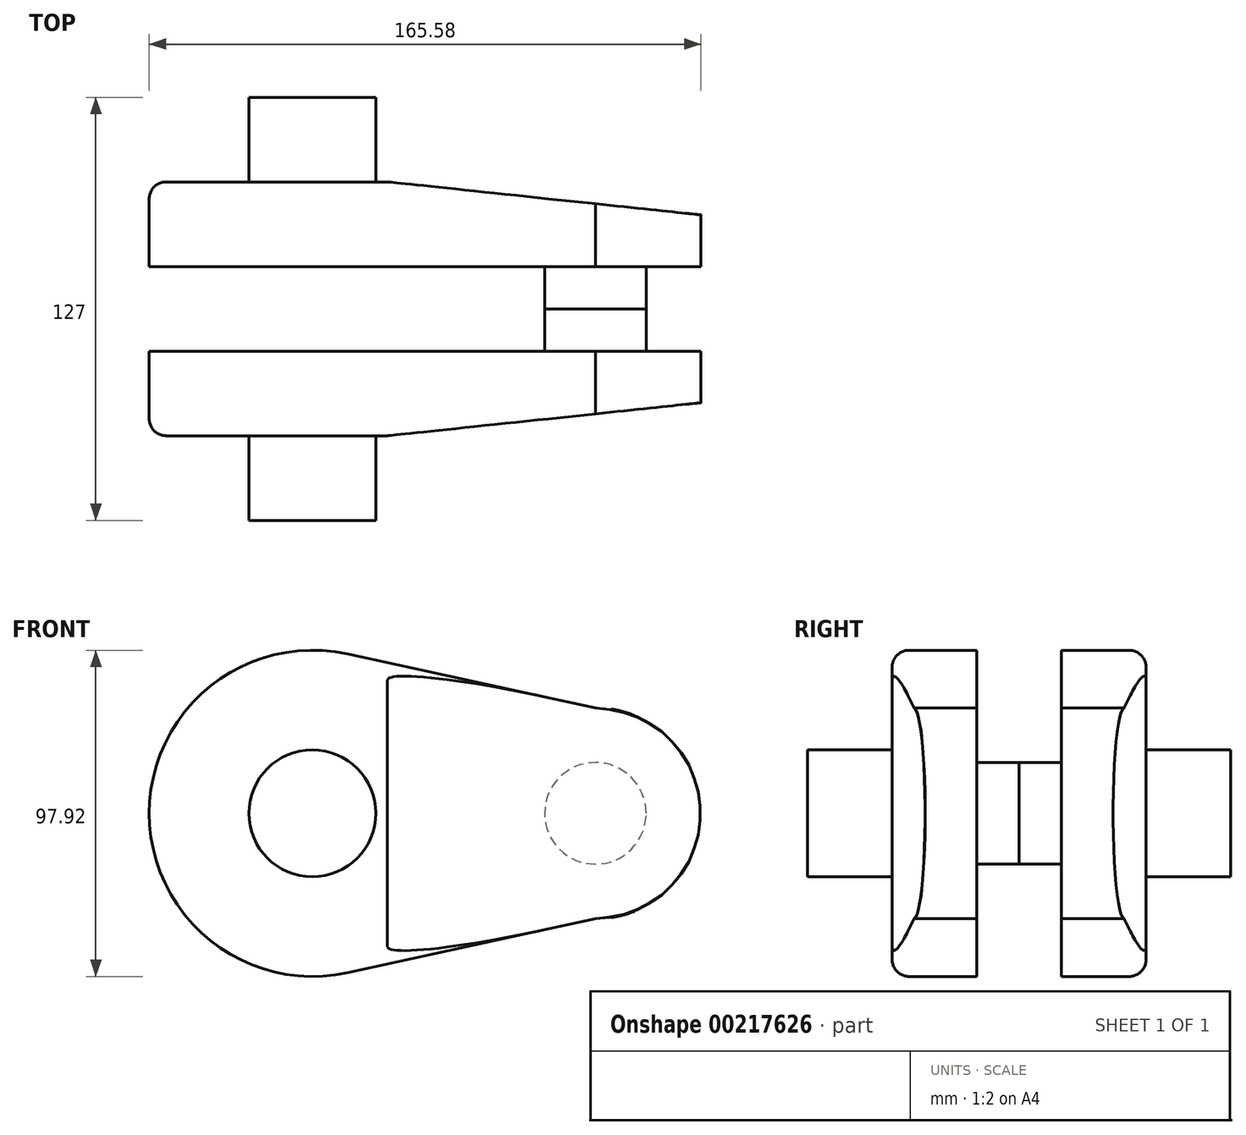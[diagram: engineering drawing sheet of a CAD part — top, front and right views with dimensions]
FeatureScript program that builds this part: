
annotation { "Feature Type Name" : "Feature", "Feature Type Description" : "" }
export const myFeature = defineFeature(function(context is Context, id is Id, definition is map)
    precondition{}
    {
        {
            var Q0;
            Q0=qCreatedBy(makeId("Front.planeOp"),FACE);
            var sketch = newSketch(context, id + "F0", { "sketchPlane" : qUnion([Q0])});
            skArc(sketch, "E0", {"start": v(10.39, 47.85) * mm, "mid": v(-48.96, 0) * mm, "end": v(10.39, -47.85) * mm});
            skArc(sketch, "E1", {"start": v(84.96, -31.65) * mm, "mid": v(116.62, 0) * mm, "end": v(84.96, 31.65) * mm});
            skLineSegment(sketch, "E2", {"start": v(84.96, 31.65) * mm, "end": v(10.39, 47.85) * mm});
            skLineSegment(sketch, "E3", {"start": v(84.96, -31.65) * mm, "end": v(10.39, -47.85) * mm});
            skSolve(sketch);
        }
        {
            var Q0;
            Q0 = qSketchRegion(id + "F0", true);
            extrude(context, id + "F1", {"entities" : qUnion([Q0]), "depth" : 25.4 * mm});
        }
        {
            var Q0;
            Q0=makeQuery(id+"F1.opExtrude","CAP_FACE",FACE,{"disambiguationData":[OSD([sQuery(id+"F0.wireOp",EDGE,"E0"),sQuery(id+"F0.wireOp",EDGE,"E1"),sQuery(id+"F0.wireOp",EDGE,"E2"),sQuery(id+"F0.wireOp",EDGE,"E3")])],"isStart":false});
            var sketch = newSketch(context, id + "F2", { "sketchPlane" : qUnion([Q0])});
            skCircle(sketch, "E4", {"center": v(84.96, 0) * mm, "radius": 15.24 * mm});
            skSolve(sketch);
        }
        {
            var Q0;
            Q0=makeQuery(id+"F2.imprint","IMPRINT",FACE,{"disambiguationData":[TD([[makeQuery(id+"F2.imprint","IMPRINT",EDGE,{"derivedFrom":sQuery(id+"F2.wireOp",EDGE,"E4")}),1.0]])]});
            extrude(context, id + "F3", {"entities" : qUnion([Q0]), "operationType" : NewBodyOperationType.ADD, "depth" : 12.7 * mm});
        }
        {
            var Q0;
            Q0=makeQuery(id+"F1.opExtrude","CAP_FACE",FACE,{"disambiguationData":[OSD([sQuery(id+"F0.wireOp",EDGE,"E0"),sQuery(id+"F0.wireOp",EDGE,"E1"),sQuery(id+"F0.wireOp",EDGE,"E2"),sQuery(id+"F0.wireOp",EDGE,"E3")])],"isStart":true});
            var sketch = newSketch(context, id + "F4", { "sketchPlane" : qUnion([Q0])});
            skCircle(sketch, "E5", {"center": v(0, 0) * mm, "radius": 19.05 * mm});
            skSolve(sketch);
        }
        {
            var Q0;
            Q0 = qSketchRegion(id + "F4", true);
            extrude(context, id + "F5", {"entities" : qUnion([Q0]), "operationType" : NewBodyOperationType.ADD, "depth" : 25.4 * mm});
        }
        {
            var Q0;
            Q0=qCreatedBy(makeId("Top.planeOp"),FACE);
            var sketch = newSketch(context, id + "F6", { "sketchPlane" : qUnion([Q0])});
            skLineSegment(sketch, "E6", {"start": v(126.43, -10.92) * mm, "end": v(22.55, 0) * mm});
            skLineSegment(sketch, "E7", {"start": v(22.55, 0) * mm, "end": v(22.55, 13.82) * mm});
            skLineSegment(sketch, "E8", {"start": v(22.55, 13.82) * mm, "end": v(126.43, 13.82) * mm});
            skLineSegment(sketch, "E9", {"start": v(126.43, 13.82) * mm, "end": v(126.43, -10.92) * mm});
            skPoint(sketch, "E10.start.orphan", {"position": v(0, -10.92) * mm});
            skSolve(sketch);
        }
        {
            var Q0;
            Q0 = qSketchRegion(id + "F6", true);
            extrude(context, id + "F7", {"entities" : qUnion([Q0]), "operationType" : NewBodyOperationType.REMOVE, "endBound" : BoundingType.SYMMETRIC, "oppositeDirection" : true, "depth" : 152.4 * mm});
        }
        {
            var Q0;
            Q0=makeQuery(id+"F7.boolean.opBoolean","INTERSECT",EDGE,{"derivedFrom":[makeQuery(id+"F1.opExtrude","SWEPT_FACE",FACE,{"disambiguationData":[OSD([sQuery(id+"F0.wireOp",EDGE,"E1")])]}),makeQuery(id+"F7.opExtrude","SWEPT_FACE",FACE,{"disambiguationData":[OSD([sQuery(id+"F6.wireOp",EDGE,"E6")])]})]});
            fillet(context, id + "F8", {"entities" : qUnion([Q0]), "radius" : 0.03 * mm, "tangentPropagation" : true, "allowEdgeOverflow" : false});
        }
        {
            var Q0;
            Q0=makeQuery(id+"F5.opExtrude","CAP_EDGE",EDGE,{"disambiguationData":[OSD([sQuery(id+"F4.wireOp",EDGE,"E5")])],"isStart":true});
            var Q1;
            Q1=makeQuery(id+"F1.opExtrude","CAP_EDGE",EDGE,{"disambiguationData":[OSD([sQuery(id+"F0.wireOp",EDGE,"E0")])],"isStart":true});
            fillet(context, id + "F9", {"entities" : qUnion([Q0, Q1]), "radius" : 5.08 * mm, "tangentPropagation" : true, "allowEdgeOverflow" : false});
        }
        {
            var Q0;
            Q0=makeQuery(id+"F1.opExtrude","SWEPT_BODY",BODY,{"disambiguationData":[OSD([sQuery(id+"F0.wireOp",EDGE,"E0"),sQuery(id+"F0.wireOp",EDGE,"E1"),sQuery(id+"F0.wireOp",EDGE,"E2"),sQuery(id+"F0.wireOp",EDGE,"E3")])]});
            var Q1;
            Q1=makeQuery(id+"F3.opExtrude","CAP_FACE",FACE,{"disambiguationData":[OSD([sQuery(id+"F2.wireOp",EDGE,"E4")])],"isStart":false});
            mirror(context, id + "F10", {"entities" : qUnion([Q0]), "mirrorPlane" : qUnion([Q1])});
        }
    });
